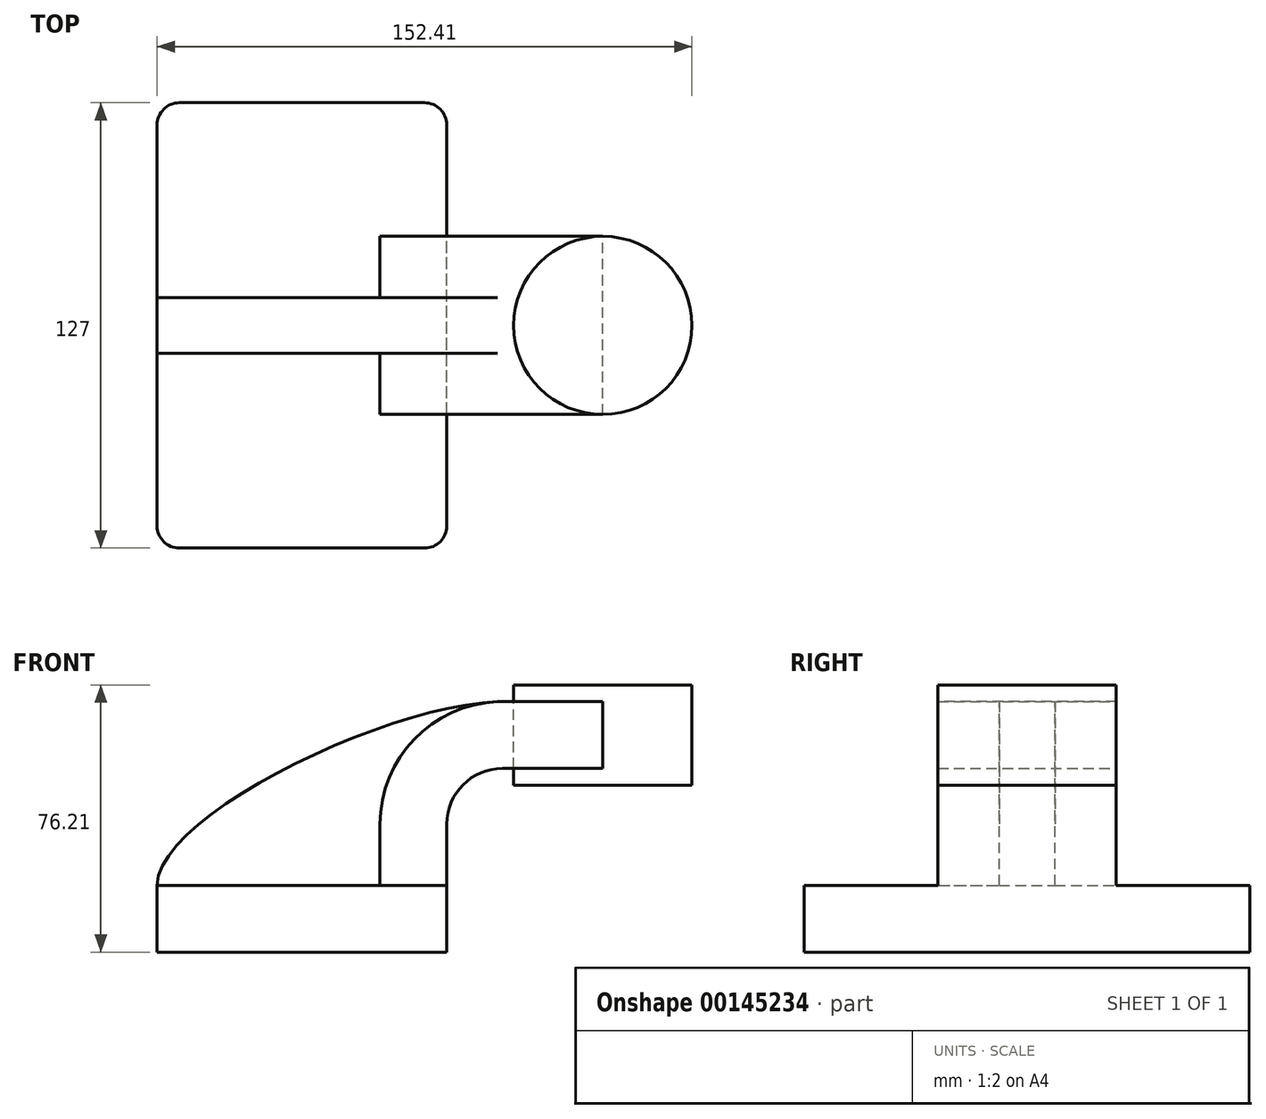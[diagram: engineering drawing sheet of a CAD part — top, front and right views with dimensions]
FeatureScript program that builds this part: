
annotation { "Feature Type Name" : "Feature", "Feature Type Description" : "" }
export const myFeature = defineFeature(function(context is Context, id is Id, definition is map)
    precondition{}
    {
        {
            var Q0;
            Q0=qCreatedBy(makeId("Front.planeOp"),FACE);
            var sketch = newSketch(context, id + "F0", { "sketchPlane" : qUnion([Q0])});
            skLineSegment(sketch, "E0.bottom", {"start": v(-41.28, 9.53) * mm, "end": v(41.28, 9.53) * mm});
            skLineSegment(sketch, "E0.top", {"start": v(-41.28, -9.53) * mm, "end": v(41.28, -9.53) * mm});
            skLineSegment(sketch, "E0.left", {"start": v(-41.28, 9.52) * mm, "end": v(-41.28, -9.53) * mm});
            skLineSegment(sketch, "E0.right", {"start": v(41.28, 9.53) * mm, "end": v(41.28, -9.52) * mm});
            skPoint(sketch, "E0.middle", {"position": v(0, 0) * mm});
            skLineSegment(sketch, "E1.bottom", {"start": v(111.12, 38.1) * mm, "end": v(60.32, 38.1) * mm});
            skLineSegment(sketch, "E1.top", {"start": v(111.12, 66.68) * mm, "end": v(60.32, 66.68) * mm});
            skLineSegment(sketch, "E1.left", {"start": v(111.12, 38.1) * mm, "end": v(111.12, 66.68) * mm});
            skLineSegment(sketch, "E1.right", {"start": v(60.32, 38.1) * mm, "end": v(60.32, 66.68) * mm});
            skPoint(sketch, "E1.middle", {"position": v(85.72, 52.39) * mm});
            skLineSegment(sketch, "E2", {"start": v(41.28, 9.53) * mm, "end": v(41.28, 26.99) * mm});
            skArc(sketch, "E3", {"start": v(41.27, 26.99) * mm, "mid": v(45.92, 38.21) * mm, "end": v(57.15, 42.86) * mm});
            skLineSegment(sketch, "E4", {"start": v(57.15, 42.86) * mm, "end": v(85.72, 42.86) * mm});
            skLineSegment(sketch, "E5.0", {"start": v(57.15, 61.91) * mm, "end": v(85.72, 61.91) * mm});
            skArc(sketch, "E5.1", {"start": v(22.22, 26.99) * mm, "mid": v(32.45, 51.68) * mm, "end": v(57.15, 61.91) * mm});
            skLineSegment(sketch, "E5.2", {"start": v(22.23, 9.52) * mm, "end": v(22.23, 26.99) * mm});
            skFitSpline(sketch, "E6", {"points": [v(-41.28, 9.52) * mm, v(57.15, 61.91) * mm], "startDerivative": vector(0.96, 61.52) * mm, "endDerivative": vector(93.25, 0.51) * mm});
            skLineSegment(sketch, "E7", {"start": v(85.72, 66.68) * mm, "end": v(85.72, 38.1) * mm});
            skSolve(sketch);
        }
        {
            var Q0;
            Q0=makeQuery(id+"F0.imprint","IMPRINT",FACE,{"disambiguationData":[TD([[makeQuery(id+"F0.imprint","IMPRINT",EDGE,{"derivedFrom":sQuery(id+"F0.wireOp",EDGE,"E0.bottom")}),-1.0]])]});
            extrude(context, id + "F1", {"entities" : qUnion([Q0]), "endBound" : BoundingType.SYMMETRIC, "depth" : 127 * mm});
        }
        {
            var Q0;
            {var subQ1=sQuery(id+"F0.wireOp",EDGE,"E2");Q0=makeQuery(id+"F0.imprint","IMPRINT",FACE,{"disambiguationData":[TD([[makeQuery(id+"F0.imprint","IMPRINT",EDGE,{"derivedFrom":subQ1}),1.0]])]});}
            var Q1;
            {var subQ5=sQuery(id+"F0.wireOp",EDGE,"r4awT23H-lMDB-Zy09-Pe6M-P6Rx6B0QqxSK");Q1=makeQuery(id+"F0.imprint","IMPRINT",FACE,{"disambiguationData":[TD([[makeQuery(id+"F0.imprint","IMPRINT",EDGE,{"derivedFrom":subQ5}),-1.0]])]});}
            var Q2;
            {var subQ0=sQuery(id+"F0.wireOp",EDGE,"E4");var subQ1=sQuery(id+"F0.wireOp",EDGE,"E1.right");var subQ2=makeQuery(id+"F0.imprint","INTERSECT",VERTEX,{"derivedFrom":[subQ1,subQ0]});Q2=makeQuery(id+"F0.imprint","IMPRINT",FACE,{"disambiguationData":[TD([[makeQuery(id+"F0.imprint","IMPRINT",EDGE,{"disambiguationData":[TD([[subQ2,-1.0]])],"derivedFrom":subQ1}),-1.0]])]});}
            extrude(context, id + "F2", {"entities" : qUnion([Q0, Q1, Q2]), "operationType" : NewBodyOperationType.ADD, "endBound" : BoundingType.SYMMETRIC, "depth" : 50.8 * mm});
        }
        {
            var Q0;
            {var subQ3=sQuery(id+"F0.wireOp",EDGE,"E5.2");Q0=makeQuery(id+"F0.imprint","IMPRINT",FACE,{"disambiguationData":[TD([[makeQuery(id+"F0.imprint","IMPRINT",EDGE,{"derivedFrom":subQ3}),1.0]])]});}
            extrude(context, id + "F3", {"entities" : qUnion([Q0]), "operationType" : NewBodyOperationType.ADD, "endBound" : BoundingType.SYMMETRIC, "depth" : 15.88 * mm});
        }
        {
            var Q0;
            {var subQ4=sQuery(id+"F0.wireOp",EDGE,"E1.left");Q0=makeQuery(id+"F0.imprint","IMPRINT",FACE,{"disambiguationData":[TD([[makeQuery(id+"F0.imprint","IMPRINT",EDGE,{"derivedFrom":subQ4}),1.0]])]});}
            var Q1;
            Q1=sQuery(id+"F0.wireOp",EDGE,"E7");
            revolve(context, id + "F4", {"entities" : qUnion([Q0]), "axis" : qUnion([Q1]), "revolveType" : RevolveType.FULL});
        }
        {
            var Q0;
            Q0=makeQuery(id+"F1.opExtrude","CAP_EDGE",EDGE,{"disambiguationData":[OSD([sQuery(id+"F0.wireOp",EDGE,"E0.right")])],"isStart":false});
            var Q1;
            Q1=makeQuery(id+"F1.opExtrude","CAP_EDGE",EDGE,{"disambiguationData":[OSD([sQuery(id+"F0.wireOp",EDGE,"E0.left")])],"isStart":false});
            var Q2;
            Q2=makeQuery(id+"F1.opExtrude","CAP_EDGE",EDGE,{"disambiguationData":[OSD([sQuery(id+"F0.wireOp",EDGE,"E0.right")])],"isStart":true});
            var Q3;
            Q3=makeQuery(id+"F1.opExtrude","CAP_EDGE",EDGE,{"disambiguationData":[OSD([sQuery(id+"F0.wireOp",EDGE,"E0.left")])],"isStart":true});
            fillet(context, id + "F5", {"entities" : qUnion([Q0, Q1, Q2, Q3]), "radius" : 6.35 * mm, "tangentPropagation" : true, "allowEdgeOverflow" : false});
        }
    });
